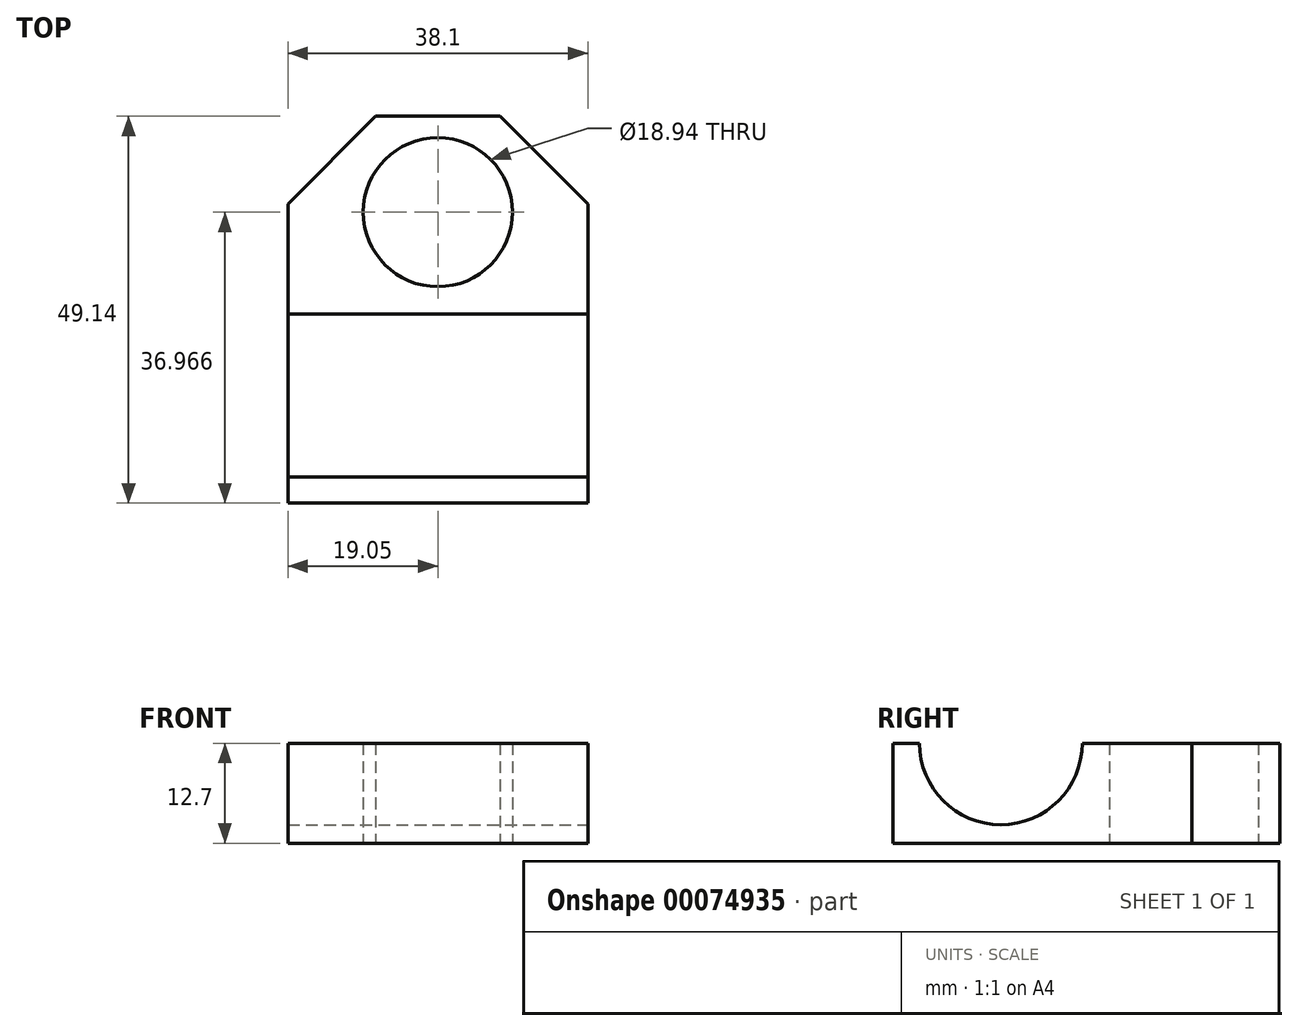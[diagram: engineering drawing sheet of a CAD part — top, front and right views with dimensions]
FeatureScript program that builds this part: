
annotation { "Feature Type Name" : "Feature", "Feature Type Description" : "" }
export const myFeature = defineFeature(function(context is Context, id is Id, definition is map)
    precondition{}
    {
        {
            var Q0;
            Q0=qCreatedBy(makeId("Top.planeOp"),FACE);
            var sketch = newSketch(context, id + "F0", { "sketchPlane" : qUnion([Q0])});
            skLineSegment(sketch, "E0.0", {"start": v(-7.9, 49.14) * mm, "end": v(7.9, 49.14) * mm});
            skLineSegment(sketch, "E0.1", {"start": v(7.9, 49.14) * mm, "end": v(19.05, 37.98) * mm});
            skLineSegment(sketch, "E0.2", {"start": v(19.05, 37.98) * mm, "end": v(19.05, 30.09) * mm});
            skLineSegment(sketch, "E0.7", {"start": v(-19.05, 37.98) * mm, "end": v(-7.9, 49.14) * mm});
            skLineSegment(sketch, "E1", {"start": v(-19.05, 30.09) * mm, "end": v(-19.05, 37.98) * mm});
            skLineSegment(sketch, "E2", {"start": v(-19.05, 30.09) * mm, "end": v(-19.05, 0) * mm});
            skLineSegment(sketch, "E3", {"start": v(-19.05, 0) * mm, "end": v(19.05, 0) * mm});
            skLineSegment(sketch, "E4", {"start": v(19.05, 0) * mm, "end": v(19.05, 30.09) * mm});
            skCircle(sketch, "E5", {"center": v(0, 36.97) * mm, "radius": 9.47 * mm});
            skSolve(sketch);
        }
        {
            var Q0;
            Q0 = qSketchRegion(id + "F0", true);
            extrude(context, id + "F1", {"entities" : qUnion([Q0]), "endBound" : BoundingType.SYMMETRIC, "depth" : 12.7 * mm});
        }
        {
            var Q0;
            Q0=makeQuery(id+"F1.opExtrude","SWEPT_FACE",FACE,{"disambiguationData":[OSD([sQuery(id+"F0.wireOp",EDGE,"E0.2"),sQuery(id+"F0.wireOp",EDGE,"E4")])]});
            var sketch = newSketch(context, id + "F2", { "sketchPlane" : qUnion([Q0])});
            skArc(sketch, "E6", {"start": v(3.34, 6.35) * mm, "mid": v(13.7, -4) * mm, "end": v(24.04, 6.35) * mm});
            skLineSegment(sketch, "E7", {"start": v(24.04, 6.35) * mm, "end": v(3.34, 6.35) * mm});
            skPoint(sketch, "E8", {"position": v(31.84, 0) * mm});
            skSolve(sketch);
        }
        {
            var Q0;
            Q0 = qSketchRegion(id + "F2", true);
            extrude(context, id + "F3", {"entities" : qUnion([Q0]), "operationType" : NewBodyOperationType.REMOVE, "oppositeDirection" : true, "depth" : 38.1 * mm});
        }
    });
